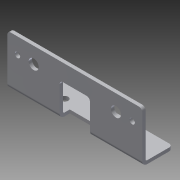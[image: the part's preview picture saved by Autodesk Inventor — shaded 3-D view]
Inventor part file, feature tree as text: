
AUTODESK INVENTOR PART (.ipt)
format: ipt  version: 2014 SP1 (Build 180222100, 222)  size: 271,360 bytes
history: native  units: in
note: dims shown in document units (in); Inventor stores cm internally (conversion verified against a paired STEP export)
features: other x7, sketch x6, sheet_metal_op x3, reference x3, chamfer x2
ambient origin geometry x8: Origin, YZ Plane, XZ Plane, XY Plane, X Axis, Y Axis, Z Axis, Center Point
bodies: Solid1 (feature_tree)
feature tree (21):
  sheet_metal_op  "Face1"
  sheet_metal_op  "Flange1"
  chamfer  "Corner Round1"
  chamfer  "Corner Round2"
  sketch  "Sketch1"  dims[d0=5.0in]
  other  "Plate1"
  sketch  "Sketch2"  dims[d1=1.125in]
  other  "Plate2"
  sheet_metal_op  "Bend1"
  sketch  "Sketch3"  dims[d3=0.125in]
  sketch  "Sketch4"  dims[d4=0.125in]
  sketch  "Sketch5"  dims[d5=0.0625in]
  sketch  "Sketch6"  dims[d6=0.25in d7=0.125in d8=1.875in d9=90.0deg d10=0.05in d11=0.5in d12=0.125in d13=0.125in d18=1.125in d20=0.375in d21=0.0in d22=0.625in d23=0.26in d24=0.26in d25=2.0in d26=1.0in d27=0.125in d28=0.0in d29=0.125in d30=0.125in d31=0.0in d32=0.125in d33=0.0in d34=0.125in d35=0.375in d36=0.375in d37=1.25in d2=0.25in]
  reference  "Reference7"
  reference  "Reference14"
  reference  "Reference15"
  other  "Cut1"
  other  "Cut2"
  other  "Cut3"
  other  "Cut4"
  other  "Definition1"
